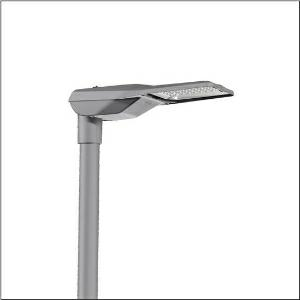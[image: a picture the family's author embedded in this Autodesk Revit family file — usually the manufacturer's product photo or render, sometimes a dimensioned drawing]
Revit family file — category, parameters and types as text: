
# Revit family: streetlight_sl_21_iq_mini___p0_8a_5xe2u31v08jb_63ec
name_source: partatom
category: Lighting Fixtures
units: mm (PartAtom-declared; Revit-internal decimal feet)

## family parameters
Cut with Voids When Loaded = No
Host = Face
Light Source = No
Part Type = Normal
Room Calculation Point = No
Round Connector Dimension = Use Diameter
Shared = No

## types (1)
- --- (1 x LED, 11310 lm, 72.5 W, 3000K)
    Apparent Load = 73 VA
    CIE Flux Codes = 36 69 97 100 100
    Color Rendering = 70
    Color Temperature = 3000K
    Default Elevation = 1800 mm
    Description = Streetlight SL 21 iQ mini, mast luminaire, primary light control with lens, of PMMA, primary optical cover: cover, of toughened safety glass, transparent, light distribution: P0.8a, light emission: direct distribution, primary light characteristic: asymmetric, installation type: post-top, side-entry, LED, High Power LED, rated luminous flux: 11.310lm, luminous efficacy: 156lm/W, light colour: 730, colour temperature: 3000K, control gear: iQ-Street Remote, D4i with power reduction, control: pre-setting: logarithmic dimming characteristic, Street-Remote, Auto-Match, Temp-Guard, Lumen-Switch, Night-Set, Smart-Wire, Light-Fading, Desk-Remote (wireless, voltage-free reading and setting of iQ features in the workshop via application-optimized NFC function/RFID function), optimised constant luminous flux control (CLO 2.0), mains connection: 220..240V, AC, 50/60Hz, start of lifetime: 73W, end of service life: 76W, reduction: 33W, luminaire housing, of diecast aluminium, powder-coated, SITECO metallic grey (DB 702S), corrosivity category C5 high according to DIN EN ISO 12944, please order mast flange separately, inclination adjustable: 0°, 5°, 10°, 15°, sealing non-destructively replaceable, multi-level sealing system, length: 628mm, width: 235mm, height: 110mm, mast flange for spigot size: 42mm (side-entry): 5XC10008XM4, 60/48mm (side-entry/post-top): 5XC10108XM2, 76/60mm (side-entry/post-top): 5XC10108XM1, mounting height: 4..8m, Smart Interface above, protection rating (complete): IP66, insulation class (complete): insulation class II (safety insulation), certification: CE, ENEC, ENEC+, VDE, impact resistance: IK10, permissible operating ambient temperature for outdoor applications: -40..+50°C, standard-compliant lighting for roads and squares, packaging unit: 1 piece

Light Distribution: P0.8a
    Height = 110 mm
    Lamp = 1 x LED
    Lamp Light Flux = 11310 lm
    Lamp Power = 72.5 W
    Lamp count = 1
    Length = 625 mm
    Luminous efficacy = 156 lm/W
    Manufacturer = Siteco
    ModVariant = No
    Model = 5XE2U31V08JB
    Number of Poles = 1
    OnlyDefault = Yes
    Power Factor = 1
    Product Name = Streetlight SL 21 iQ mini | P0.8a
    Product group = mast luminaire | pylon top
    ProductGroupID = 6100
    Protection Class = Protection class II
    Protection Degree = IP 66
    RLX_Detail_Level = 1
    RLX_Emergency_Light_Flux = 0 lm
    RLX_Emergency_Type = 0
    RLX_Emergency_Type_DB = No
    RlxData = <blob elided: 92245 chars, md5=7554c8e5>
    Socket = socket
    Standby Power = 0 W
    System Light Flux = 11310 lm
    System Power = 73 W
    Type Comments = factory setting: luminous flux: 100 % | dim-lin: 254 | 755 mA
    Type Image = l_1003515.jpg
    URL = http://relux.com
    VarID = @adj_079877
    Voltage = 0 V
    Weight = 0.00 kg
    Width = 234 mm

## geometry (parser evidence)
native form markers: Blend x4, Sweep x12
no freeform markers — native parametric forms only
